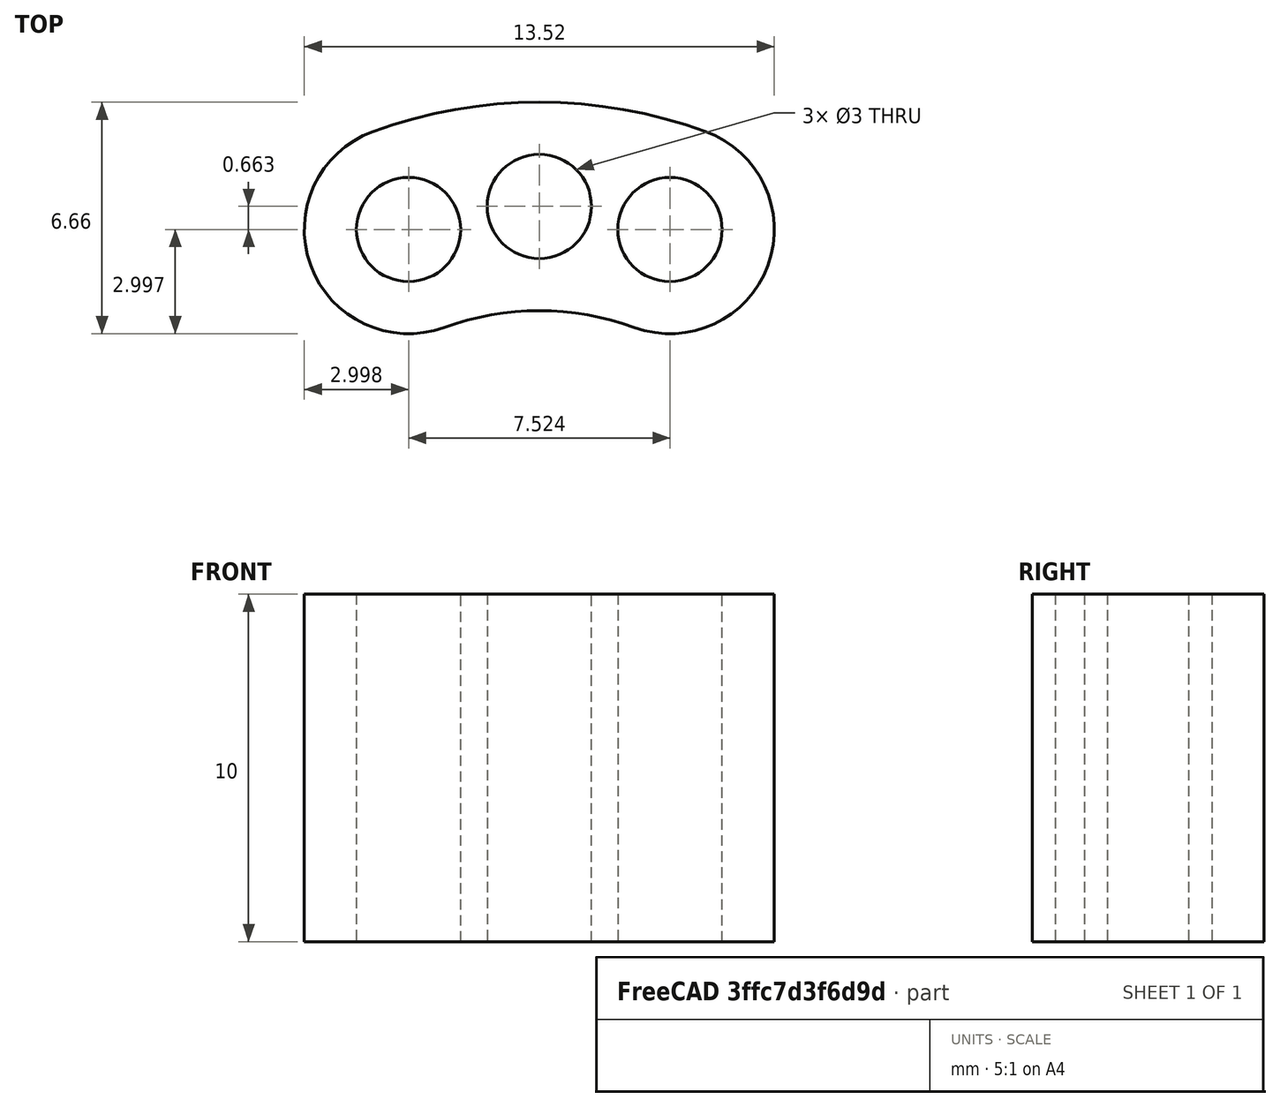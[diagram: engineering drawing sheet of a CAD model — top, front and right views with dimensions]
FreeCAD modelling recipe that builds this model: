
FCSTD DOCUMENT  (FreeCAD 0.21R33668 +26 (Git))
Label: supporter
License: All rights reserved
LicenseURL: http://en.wikipedia.org/wiki/All_rights_reserved
objects: Sketcher::SketchObject×1, PartDesign::Pad×1, PartDesign::Body×1
note: 4 computed .brp shape members not serialized (recipe doc carries the construction recipe); baked Part::Feature solids carry a one-line shape summary decoded from their .brp

FEATURE [Sketcher::SketchObject] Sketch
  FullyConstrained = true
  MapMode = 5
  Support = -> [XY_Plane]
  sketch-geometry (13):
    g0: Circle CenterX=0 CenterY=0 CenterZ=0 NormalX=0 NormalY=0 NormalZ=1 AngleXU=0 Radius=11
    g1: LineSegment StartX=0 StartY=0 StartZ=0 EndX=-3.76222 EndY=10.3366 EndZ=0
    g2: LineSegment StartX=0 StartY=0 StartZ=0 EndX=3.76222 EndY=10.3366 EndZ=0
    g3: LineSegment StartX=-3.76222 StartY=10.3366 StartZ=0 EndX=3.76222 EndY=10.3366 EndZ=0
    g4: ArcOfCircle CenterX=-3.76222 CenterY=10.3366 CenterZ=0 NormalX=0 NormalY=0 NormalZ=1 AngleXU=0 Radius=3 StartAngle=1.91986 EndAngle=5.06145
    g5: ArcOfCircle CenterX=3.76222 CenterY=10.3366 CenterZ=0 NormalX=0 NormalY=0 NormalZ=1 AngleXU=0 Radius=3 StartAngle=4.36332 EndAngle=7.50492
    g6: ArcOfCircle CenterX=0 CenterY=0 CenterZ=0 NormalX=0 NormalY=0 NormalZ=1 AngleXU=0 Radius=8 StartAngle=1.22173 EndAngle=1.91986
    g7: ArcOfCircle CenterX=0 CenterY=0 CenterZ=0 NormalX=0 NormalY=0 NormalZ=1 AngleXU=0 Radius=14 StartAngle=1.22173 EndAngle=1.91986
    g8: Circle CenterX=-3.76222 CenterY=10.3366 CenterZ=0 NormalX=0 NormalY=0 NormalZ=1 AngleXU=0 Radius=1.5
    g9: Circle CenterX=3.76222 CenterY=10.3366 CenterZ=0 NormalX=0 NormalY=0 NormalZ=1 AngleXU=0 Radius=1.5
    g10: LineSegment StartX=0 StartY=0 StartZ=0 EndX=0 EndY=11 EndZ=0
    g11: Circle CenterX=0 CenterY=11 CenterZ=0 NormalX=0 NormalY=0 NormalZ=1 AngleXU=0 Radius=1.5
    g12: Circle CenterX=0 CenterY=11 CenterZ=0 NormalX=0 NormalY=0 NormalZ=1 AngleXU=0 Radius=3
  constraints (29):
    c: Coincident(g0,g-1)
    c: Diameter(g0) = 22
    c: Coincident(g1,g0)
    c: PointOnObject(g1,g0)
    c: Coincident(g2,g1)
    c: Coincident(g3,g1)
    c: Coincident(g3,g2)
    c: Horizontal(g3)
    c: Angle(g2,g-2) = 0.349066
    c: Coincident(g4,g1)
    c: Coincident(g5,g2)
    c: Coincident(g6,g0)
    c: Coincident(g7,g6)
    c: Tangent(g7,g5) = -1.5708
    c: Tangent(g7,g4) = -1.5708
    c: Tangent(g6,g4) = 1.5708
    c: Tangent(g6,g5) = 1.5708
    c: Diameter(g4) = 6
    c: Coincident(g8,g4)
    c: Coincident(g9,g5)
    c: Coincident(g10,g6)
    c: PointOnObject(g10,g0)
    c: Vertical(g10)
    c: Coincident(g11,g10)
    c: Equal(g8,g11)
    c: Equal(g11,g9)
    c: Diameter(g8) = 3
    c: Coincident(g12,g11)
    c: Equal(g12,g4)
FEATURE [PartDesign::Pad] Pad
  Direction = (0,0,1)
  Length = 10
  Length2 = 10
  Profile = -> Sketch
  ReferenceAxis = -> Sketch [N_Axis]
  Type = 0
FEATURE [PartDesign::Body] Body
  Group = -> [Sketch,Pad]
  Origin = -> Origin
  Tip = -> Pad
